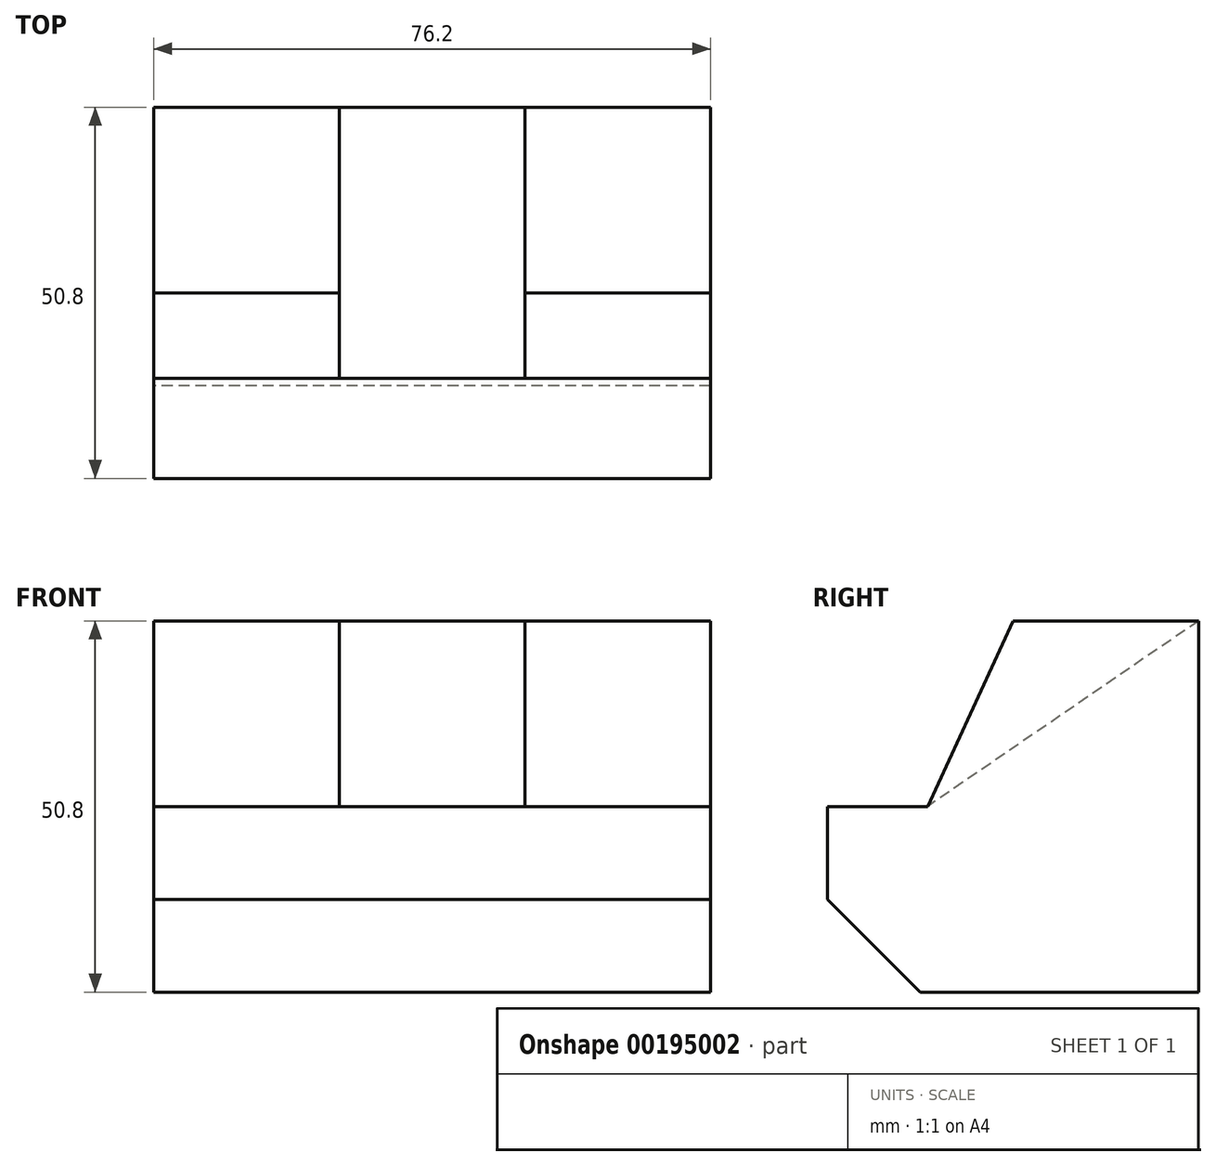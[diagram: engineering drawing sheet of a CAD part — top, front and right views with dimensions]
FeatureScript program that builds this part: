
annotation { "Feature Type Name" : "Feature", "Feature Type Description" : "" }
export const myFeature = defineFeature(function(context is Context, id is Id, definition is map)
    precondition{}
    {
        {
            var Q0;
            Q0=qCreatedBy(makeId("Right.planeOp"),FACE);
            var sketch = newSketch(context, id + "F0", { "sketchPlane" : qUnion([Q0])});
            skLineSegment(sketch, "E0", {"start": v(0, 0) * mm, "end": v(-38.1, 0) * mm});
            skLineSegment(sketch, "E1", {"start": v(-38.1, 0) * mm, "end": v(-50.8, 12.7) * mm});
            skLineSegment(sketch, "E2", {"start": v(-50.8, 12.7) * mm, "end": v(-50.8, 25.4) * mm});
            skLineSegment(sketch, "E3", {"start": v(-37.1, 25.4) * mm, "end": v(-50.8, 25.4) * mm});
            skLineSegment(sketch, "E4", {"start": v(-37.1, 25.4) * mm, "end": v(-25.4, 50.8) * mm});
            skLineSegment(sketch, "E5", {"start": v(-25.4, 50.8) * mm, "end": v(0, 50.8) * mm});
            skLineSegment(sketch, "E6", {"start": v(0, 0) * mm, "end": v(0, 50.8) * mm});
            skSolve(sketch);
        }
        {
            var Q0;
            Q0 = qSketchRegion(id + "F0", true);
            extrude(context, id + "F1", {"entities" : qUnion([Q0]), "depth" : 76.2 * mm});
        }
        {
            var Q0;
            Q0=makeQuery(id+"F1.opExtrude","CAP_FACE",FACE,{"disambiguationData":[OSD([sQuery(id+"F0.wireOp",EDGE,"E0"),sQuery(id+"F0.wireOp",EDGE,"E1"),sQuery(id+"F0.wireOp",EDGE,"E2"),sQuery(id+"F0.wireOp",EDGE,"E3"),sQuery(id+"F0.wireOp",EDGE,"E4"),sQuery(id+"F0.wireOp",EDGE,"E5"),sQuery(id+"F0.wireOp",EDGE,"E6")])],"isStart":true});
            var Q1;
            Q1=makeQuery(id+"F1.opExtrude","CAP_FACE",FACE,{"disambiguationData":[OSD([sQuery(id+"F0.wireOp",EDGE,"E0"),sQuery(id+"F0.wireOp",EDGE,"E1"),sQuery(id+"F0.wireOp",EDGE,"E2"),sQuery(id+"F0.wireOp",EDGE,"E3"),sQuery(id+"F0.wireOp",EDGE,"E4"),sQuery(id+"F0.wireOp",EDGE,"E5"),sQuery(id+"F0.wireOp",EDGE,"E6")])],"isStart":false});
            cPlane(context, id + "F2", {"entities" : qUnion([Q0, Q1]), "cplaneType" : CPlaneType.MID_PLANE, "offset" : 25.4 * mm, "width" : 152.4 * mm, "height" : 152.4 * mm});
        }
        {
            var Q0;
            Q0=qCreatedBy(id+"F2.planeOp",FACE);
            var sketch = newSketch(context, id + "F3", { "sketchPlane" : qUnion([Q0])});
            skLineSegment(sketch, "E7", {"start": v(0, 50.8) * mm, "end": v(37.1, 25.4) * mm});
            skLineSegment(sketch, "E8", {"start": v(37.1, 25.4) * mm, "end": v(25.4, 50.8) * mm});
            skLineSegment(sketch, "E9", {"start": v(25.4, 50.8) * mm, "end": v(0, 50.8) * mm});
            skSolve(sketch);
        }
        {
            var Q0;
            Q0 = qSketchRegion(id + "F3", true);
            extrude(context, id + "F4", {"entities" : qUnion([Q0]), "operationType" : NewBodyOperationType.REMOVE, "oppositeDirection" : true, "depth" : 12.7 * mm, "hasSecondDirection" : true, "secondDirectionOppositeDirection" : false, "secondDirectionDepth" : 12.7 * mm});
        }
    });
